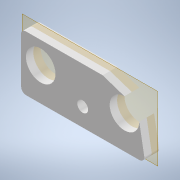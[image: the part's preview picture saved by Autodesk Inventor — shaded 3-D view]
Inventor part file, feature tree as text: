
AUTODESK INVENTOR PART (.ipt)
format: ipt  version: 2022.3 (Build 263350000, 350)  size: 169,472 bytes
history: native  units: mm
features: other x5, extrude x4, sketch x4, reference x3, plane x1, projected_geometry x1
ambient origin geometry x8: Origin, YZ Plane, XZ Plane, XY Plane, X Axis, Y Axis, Z Axis, Center Point
bodies: Solid1 (feature_tree)
feature tree (18):
  plane  "Work Plane1"
  extrude  "Extrusion1"  Depth=4.0mm TaperAngle=0.0deg
  extrude  "Extrusion2"  Depth=0.5mm
  extrude  "Extrusion3"  Depth=3.0mm TaperAngle=0.0deg
  extrude  "Extrusion4"  [1 undecoded]
  sketch  "Sketch1"  dims[d0=2.2mm d1=4.0mm d2=0.0mm]
  reference  "Reference1"
  sketch  "Sketch2"  dims[d3=4.0mm d4=0.0mm d5=0.5mm]
  reference  "Reference2"
  sketch  "Sketch3"  dims[d6=10.0mm d7=0.0mm d8=3.0mm d9=0.0mm]
  projected_geometry  "Projected Loop1"
  sketch  "Sketch4"
  reference  "Reference3"
  other  "<userpath>\Documents\Inventor\NanoSumo\NanoSumo_part1.iam"
  other  "NanoSumo_part1.iam"
  other  "bok:2"
  other  "bok:1"
  other  "Assembly3"
note: 1 required parameter value undecoded (feature->parameter linkage not recoverable at this tier; creation-order binding heuristic only, values carry confidence <= 0.55)
